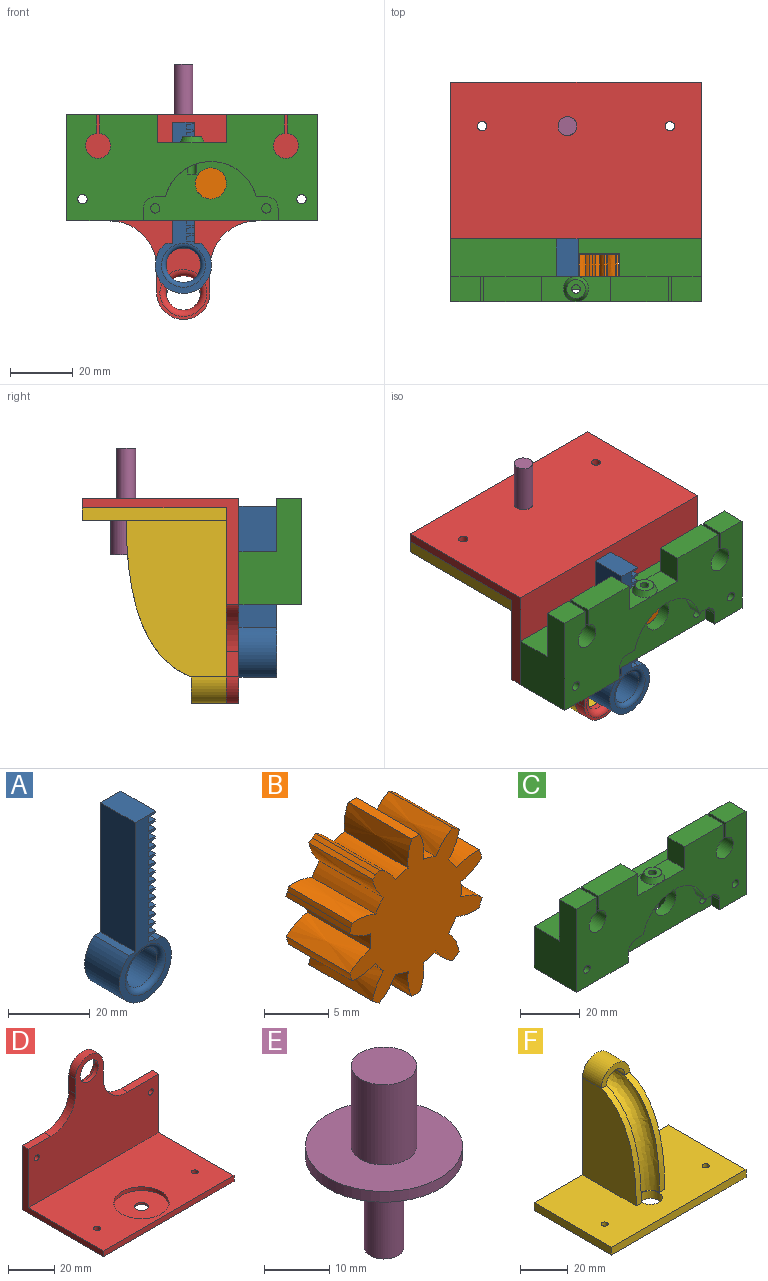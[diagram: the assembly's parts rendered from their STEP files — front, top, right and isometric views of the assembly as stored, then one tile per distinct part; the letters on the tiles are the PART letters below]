
ASSEMBLY  parts=6 mates=12
PART A: 71 faces, bbox 18x12x54.7 mm
  f0: plane 38.7x12mm, normal (1,0,0), area 228.2mm2, adj f1,f2,f4,f5,f6,f8,f9,f10
  f1: plane 54.7x18mm, normal (0,-1,0), area 288.5mm2, adj f0,f3,f4,f5,f6,f7,f9,f10
  f2: plane 54.7x18mm, normal (0,1,0), area 356mm2, adj f0,f3,f4,f65,f66,f68,f70
  f3: plane 38.7x12mm, normal (-1,0,0), area 464.4mm2, adj f1,f2,f4,f65
  f4: plane 12x7mm, normal (0,0,1), area 84mm2, adj f0,f1,f2,f3
  f5: plane 7.5x2.5mm, normal (0.12,0,0.99), area 18.9mm2, adj f0,f1,f7,f8
  f6: plane 7.5x2.5mm, normal (0.12,0,-0.99), area 18.9mm2, adj f0,f1,f7,f8
  f7: plane 7.5x1.5mm, normal (1,0,0), area 11.2mm2, adj f1,f5,f6,f8
  f8: plane 2.5x2.1mm, normal (0,-1,0), area 4.5mm2, adj f0,f5,f6,f7
  f9: plane 7.5x2.5mm, normal (0.12,0,0.99), area 18.9mm2, adj f0,f1,f11,f12
  f10: plane 7.5x2.5mm, normal (0.12,0,-0.99), area 18.9mm2, adj f0,f1,f11,f12
  f11: plane 7.5x1.5mm, normal (1,0,0), area 11.2mm2, adj f1,f9,f10,f12
  f12: plane 2.5x2.1mm, normal (0,-1,0), area 4.5mm2, adj f0,f9,f10,f11
  f13: plane 7.5x2.5mm, normal (0.12,0,0.99), area 18.9mm2, adj f0,f1,f15,f16
  f14: plane 7.5x2.5mm, normal (0.12,0,-0.99), area 18.9mm2, adj f0,f1,f15,f16
  f15: plane 7.5x1.5mm, normal (1,0,0), area 11.2mm2, adj f1,f13,f14,f16
  f16: plane 2.5x2.1mm, normal (0,-1,0), area 4.5mm2, adj f0,f13,f14,f15
  f17: plane 7.5x2.5mm, normal (0.12,0,0.99), area 18.9mm2, adj f0,f1,f19,f20
  f18: plane 7.5x2.5mm, normal (0.12,0,-0.99), area 18.9mm2, adj f0,f1,f19,f20
  f19: plane 7.5x1.5mm, normal (1,0,0), area 11.3mm2, adj f1,f17,f18,f20
  f20: plane 2.5x2.1mm, normal (0,-1,0), area 4.5mm2, adj f0,f17,f18,f19
  f21: plane 7.5x2.5mm, normal (0.12,0,0.99), area 18.9mm2, adj f0,f1,f23,f24
  f22: plane 7.5x2.5mm, normal (0.12,0,-0.99), area 18.9mm2, adj f0,f1,f23,f24
  f23: plane 7.5x1.5mm, normal (1,0,0), area 11.2mm2, adj f1,f21,f22,f24
  f24: plane 2.5x2.1mm, normal (0,-1,0), area 4.5mm2, adj f0,f21,f22,f23
  f25: plane 7.5x2.5mm, normal (0.12,0,0.99), area 18.9mm2, adj f0,f1,f27,f28
  f26: plane 7.5x2.5mm, normal (0.12,0,-0.99), area 18.9mm2, adj f0,f1,f27,f28
  f27: plane 7.5x1.5mm, normal (1,0,0), area 11.2mm2, adj f1,f25,f26,f28
  f28: plane 2.5x2.1mm, normal (0,-1,0), area 4.5mm2, adj f0,f25,f26,f27
  f29: plane 7.5x2.5mm, normal (0.12,0,0.99), area 18.9mm2, adj f0,f1,f31,f32
  f30: plane 7.5x2.5mm, normal (0.12,0,-0.99), area 18.9mm2, adj f0,f1,f31,f32
  f31: plane 7.5x1.5mm, normal (1,0,0), area 11.3mm2, adj f1,f29,f30,f32
  f32: plane 2.5x2.1mm, normal (0,-1,0), area 4.5mm2, adj f0,f29,f30,f31
  f33: plane 7.5x2.5mm, normal (0.12,0,0.99), area 18.9mm2, adj f0,f1,f35,f36
  f34: plane 7.5x2.5mm, normal (0.12,0,-0.99), area 18.9mm2, adj f0,f1,f35,f36
  f35: plane 7.5x1.5mm, normal (1,0,0), area 11.3mm2, adj f1,f33,f34,f36
  f36: plane 2.5x2.1mm, normal (0,-1,0), area 4.5mm2, adj f0,f33,f34,f35
  f37: plane 7.5x2.5mm, normal (0.12,0,0.99), area 18.9mm2, adj f0,f1,f39,f40
  f38: plane 7.5x2.5mm, normal (0.12,0,-0.99), area 18.9mm2, adj f0,f1,f39,f40
  f39: plane 7.5x1.5mm, normal (1,0,0), area 11.3mm2, adj f1,f37,f38,f40
  f40: plane 2.5x2.1mm, normal (0,-1,0), area 4.5mm2, adj f0,f37,f38,f39
  f41: plane 7.5x2.5mm, normal (0.12,0,0.99), area 18.9mm2, adj f0,f1,f43,f44
  f42: plane 7.5x2.5mm, normal (0.12,0,-0.99), area 18.9mm2, adj f0,f1,f43,f44
  f43: plane 7.5x1.5mm, normal (1,0,0), area 11.3mm2, adj f1,f41,f42,f44
  f44: plane 2.5x2.1mm, normal (0,-1,0), area 4.5mm2, adj f0,f41,f42,f43
  f45: plane 7.5x2.5mm, normal (0.12,0,0.99), area 18.9mm2, adj f0,f1,f47,f48
  f46: plane 7.5x2.5mm, normal (0.12,0,-0.99), area 18.9mm2, adj f0,f1,f47,f48
  f47: plane 7.5x1.5mm, normal (1,0,0), area 11.3mm2, adj f1,f45,f46,f48
  f48: plane 2.5x2.1mm, normal (0,-1,0), area 4.5mm2, adj f0,f45,f46,f47
  f49: plane 7.5x2.5mm, normal (0.12,0,0.99), area 18.9mm2, adj f0,f1,f51,f52
  f50: plane 7.5x2.5mm, normal (0.12,0,-0.99), area 18.9mm2, adj f0,f1,f51,f52
  f51: plane 7.5x1.5mm, normal (1,0,0), area 11.3mm2, adj f1,f49,f50,f52
  f52: plane 2.5x2.1mm, normal (0,-1,0), area 4.5mm2, adj f0,f49,f50,f51
  f53: plane 7.5x2.5mm, normal (0.12,0,0.99), area 18.9mm2, adj f0,f1,f55,f56
  f54: plane 7.5x2.5mm, normal (0.12,0,-0.99), area 18.9mm2, adj f0,f1,f55,f56
  f55: plane 7.5x1.5mm, normal (1,0,0), area 11.2mm2, adj f1,f53,f54,f56
  f56: plane 2.5x2.1mm, normal (0,-1,0), area 4.5mm2, adj f0,f53,f54,f55
  f57: plane 7.5x2.5mm, normal (0.12,0,0.99), area 18.9mm2, adj f0,f1,f59,f60
  f58: plane 7.5x2.5mm, normal (0.12,0,-0.99), area 18.9mm2, adj f0,f1,f59,f60
  f59: plane 7.5x1.5mm, normal (1,0,0), area 11.3mm2, adj f1,f57,f58,f60
  f60: plane 2.5x2.1mm, normal (0,-1,0), area 4.5mm2, adj f0,f57,f58,f59
  f61: plane 7.5x2.5mm, normal (0.12,0,0.99), area 18.9mm2, adj f0,f1,f63,f64
  f62: plane 7.5x2.5mm, normal (0.12,0,-0.99), area 18.9mm2, adj f0,f1,f63,f64
  f63: plane 7.5x1.5mm, normal (1,0,0), area 11.2mm2, adj f1,f61,f62,f64
  f64: plane 2.5x2.1mm, normal (0,-1,0), area 4.5mm2, adj f0,f61,f62,f63
  f65: plane 12x2.16mm, normal (0,0,1), area 25.9mm2, adj f1,f2,f3,f68
  f66: plane 12x2.16mm, normal (0,0,1), area 25.9mm2, adj f0,f1,f2,f68
  f67: cylinder r=5.5mm len=11mm, axis (0,-1,0), area 311mm2, adj f69,f70
  f68: cylinder r=9mm len=18mm, axis (0,-1,0), area 531.8mm2, adj f1,f2,f65,f66
  f69: torus R=7mm, axis (0,-1,0), area 89.5mm2, adj f1,f67
  f70: torus R=7mm, axis (0,-1,0), area 89.5mm2, adj f2,f67
PART B: 45 faces, bbox 14.5x7x15 mm
  f0: extruded ~7x2.3mm, area 18.3mm2, adj f1,f42,f43,f44
  f1: cylinder r=7.5mm len=7mm, axis (0,1,0), area 6.4mm2, adj f0,f2,f43,f44
  f2: extruded ~7x1.84mm, area 18.3mm2, adj f1,f3,f43,f44
  f3: cylinder r=5mm len=7mm, axis (0,1,0), area 10mm2, adj f2,f4,f43,f44
  f4: extruded ~7x2.56mm, area 18.3mm2, adj f3,f5,f43,f44
  f5: cylinder r=7.5mm len=7mm, axis (0,1,0), area 6.4mm2, adj f4,f6,f43,f44
  f6: extruded ~7x2.56mm, area 18.3mm2, adj f5,f7,f43,f44
  f7: cylinder r=5mm len=7mm, axis (0,1,0), area 10mm2, adj f6,f8,f43,f44
  f8: extruded ~7x1.84mm, area 18.3mm2, adj f7,f9,f43,f44
  f9: cylinder r=7.5mm len=7mm, axis (0,1,0), area 6.4mm2, adj f8,f10,f43,f44
  f10: extruded ~7x2.3mm, area 18.3mm2, adj f9,f11,f43,f44
  f11: cylinder r=5mm len=7mm, axis (0,1,0), area 10mm2, adj f10,f12,f43,f44
  f12: extruded ~7x2.56mm, area 18.3mm2, adj f11,f13,f43,f44
  f13: cylinder r=7.5mm len=7mm, axis (0,1,0), area 3.2mm2, adj f12,f14,f43,f44
  f14: plane 7x0.43mm, normal (0.95,0,-0.31), area 3.1mm2, adj f13,f15,f43,f44
  f15: extruded ~7x2.32mm, area 18.4mm2, adj f14,f16,f43,f44
  f16: cylinder r=5mm len=7mm, axis (0,1,0), area 10mm2, adj f15,f17,f43,f44
  f17: extruded ~7x2.31mm, area 18.3mm2, adj f16,f18,f43,f44
  f18: cylinder r=7.5mm len=7mm, axis (0,1,0), area 6.4mm2, adj f17,f19,f43,f44
  f19: extruded ~7x2.56mm, area 18.3mm2, adj f18,f20,f43,f44
  f20: cylinder r=5mm len=7mm, axis (0,1,0), area 10mm2, adj f19,f21,f43,f44
  f21: extruded ~7x2.3mm, area 18.3mm2, adj f20,f22,f43,f44
  f22: cylinder r=7.5mm len=7mm, axis (0,1,0), area 6.4mm2, adj f21,f23,f43,f44
  f23: extruded ~7x1.84mm, area 18.3mm2, adj f22,f24,f43,f44
  f24: cylinder r=5mm len=7mm, axis (0,1,0), area 10mm2, adj f23,f25,f43,f44
  f25: extruded ~7x2.57mm, area 18.4mm2, adj f24,f26,f43,f44
  f26: plane 7x0.9mm, normal (0,0,1), area 6.3mm2, adj f25,f27,f43,f44
  f27: extruded ~7x2.57mm, area 18.4mm2, adj f26,f28,f43,f44
  f28: cylinder r=5mm len=7mm, axis (0,1,0), area 10mm2, adj f27,f29,f43,f44
  f29: extruded ~7x1.84mm, area 18.3mm2, adj f28,f30,f43,f44
  f30: cylinder r=7.5mm len=7mm, axis (0,1,0), area 3.2mm2, adj f29,f31,f43,f44
  f31: plane 7x0.36mm, normal (-0.59,0,0.81), area 3.2mm2, adj f30,f32,f43,f44
  f32: extruded ~7x2.32mm, area 18.4mm2, adj f31,f33,f43,f44
  f33: cylinder r=5mm len=7mm, axis (0,1,0), area 10mm2, adj f32,f34,f43,f44
  f34: extruded ~7x2.56mm, area 18.3mm2, adj f33,f35,f43,f44
  f35: cylinder r=7.5mm len=7mm, axis (0,1,0), area 3.2mm2, adj f34,f36,f43,f44
  f36: plane 7x0.43mm, normal (-0.95,0,0.31), area 3.1mm2, adj f35,f37,f43,f44
  f37: extruded ~7x2.32mm, area 18.4mm2, adj f36,f38,f43,f44
  f38: cylinder r=5mm len=7mm, axis (0,1,0), area 10mm2, adj f37,f39,f43,f44
  f39: extruded ~7x2.31mm, area 18.3mm2, adj f38,f40,f43,f44
  f40: cylinder r=7.5mm len=7mm, axis (0,1,0), area 6.4mm2, adj f39,f41,f43,f44
  f41: extruded ~7x2.56mm, area 18.3mm2, adj f40,f42,f43,f44
  f42: cylinder r=5mm len=7mm, axis (0,1,0), area 10mm2, adj f0,f41,f43,f44
  f43: plane 15x14.54mm, normal (0,-1,0), area 117.2mm2, adj f0,f1,f2,f3,f4,f5,f6,f7
  f44: plane 15x14.54mm, normal (0,1,0), area 117.2mm2, adj f0,f1,f2,f3,f4,f5,f6,f7
PART C: 47 faces, bbox 80x20x34 mm
  f0: plane 80x34mm, normal (0,-1,0), area 1826mm2, adj f1,f4,f5,f6,f7,f8,f9,f10
  f1: plane 11x8mm, normal (0,0,1), area 62.9mm2, adj f0,f2,f13,f42
  f2: plane 80x34mm, normal (0,1,0), area 1315.2mm2, adj f1,f4,f5,f6,f7,f8,f9,f10
  f3: plane 43x19mm, normal (0,-1,0), area 469.2mm2, adj f4,f20,f21,f22,f23,f24,f25,f26
  f4: plane 80x20mm, normal (0,0,-1), area 1244.6mm2, adj f0,f2,f3,f5,f19,f20,f26,f31
  f5: plane 34x20mm, normal (1,0,0), area 476mm2, adj f0,f2,f4,f6,f35,f39
  f6: plane 9.5x8mm, normal (0,0,1), area 76mm2, adj f0,f2,f5,f7
  f7: plane 8x6.03mm, normal (-1,0,0), area 48.3mm2, adj f0,f2,f6,f8
  f8: cylinder r=4mm len=8mm, axis (0,1,0), area 193mm2, adj f0,f2,f7,f9
  f9: plane 8x6.03mm, normal (1,0,0), area 48.3mm2, adj f0,f2,f8,f10
  f10: plane 18.5x8mm, normal (0,0,1), area 148mm2, adj f0,f2,f9,f11
  f11: plane 9x8mm, normal (-1,0,0), area 72mm2, adj f0,f2,f10,f12
  f12: plane 11x8mm, normal (0,0,1), area 62.9mm2, adj f0,f2,f11,f42
  f13: plane 9x8mm, normal (1,0,0), area 72mm2, adj f0,f1,f2,f14
  f14: plane 18.5x8mm, normal (0,0,1), area 148mm2, adj f0,f2,f13,f15
  f15: plane 8x6.03mm, normal (-1,0,0), area 48.3mm2, adj f0,f2,f14,f16
  f16: cylinder r=4mm len=8mm, axis (0,1,0), area 193mm2, adj f0,f2,f15,f17
  f17: plane 8x6.03mm, normal (1,0,0), area 48.3mm2, adj f0,f2,f16,f18
  f18: plane 9.5x8mm, normal (0,0,1), area 76mm2, adj f0,f2,f17,f19
  f19: plane 34x20mm, normal (-1,0,0), area 476mm2, adj f0,f2,f4,f18,f30,f31
  f20: plane 4x4mm, normal (-1,0,0), area 16mm2, adj f0,f3,f4,f21
  f21: cylinder r=3.75mm len=4mm, axis (0,-1,0), area 23.6mm2, adj f0,f3,f20,f22
  f22: plane 4x3.23mm, normal (0,0,-1), area 12.9mm2, adj f0,f3,f21,f23
  f23: cylinder r=15mm len=29.05mm, axis (0,-1,0), area 154.9mm2, adj f0,f3,f22,f24,f43
  f24: plane 4x3.23mm, normal (0,0,-1), area 12.9mm2, adj f0,f3,f23,f25
  f25: cylinder r=3.75mm len=4mm, axis (0,-1,0), area 23.6mm2, adj f0,f3,f24,f26
  f26: plane 4x4mm, normal (1,0,0), area 16mm2, adj f0,f3,f4,f25
  f27: cylinder r=5mm len=10mm, axis (0,-1,0), area 125.7mm2, adj f2,f3
  f28: cylinder r=1.5mm len=4mm, axis (0,-1,0), area 37.7mm2, adj f3,f34
  f29: cylinder r=1.5mm len=4mm, axis (0,-1,0), area 37.7mm2, adj f3,f33
  f30: plane 33.75x12mm, normal (0,0,1), area 405mm2, adj f2,f19,f31,f32
  f31: plane 33.75x17mm, normal (0,1,0), area 566.7mm2, adj f4,f19,f30,f32,f46
  f32: plane 17x12mm, normal (1,0,0), area 204mm2, adj f2,f4,f30,f31
  f33: plane 3x3mm, normal (0,-1,0), area 7.1mm2, adj f29
  f34: plane 3x3mm, normal (0,-1,0), area 7.1mm2, adj f28
  f35: plane 39.25x17mm, normal (0,1,0), area 631.9mm2, adj f4,f5,f36,f39,f40,f45
  f36: plane 17x4.5mm, normal (-1,0,0), area 76.5mm2, adj f4,f35,f37,f39
  f37: plane 17x13.25mm, normal (0,-1,0), area 197mm2, adj f4,f36,f38,f39,f40
  f38: plane 17x7.5mm, normal (-1,0,0), area 127.5mm2, adj f2,f4,f37,f39
  f39: plane 39.25x12mm, normal (0,0,1), area 371.6mm2, adj f2,f5,f35,f36,f37,f38
  f40: cylinder r=3mm len=6mm, axis (0,-1,0), area 84.8mm2, adj f35,f37
  f41: plane 6x6mm, normal (0,0,1), area 22.3mm2, adj f42,f43
  f42: cone r=3mm half-angle=26.6deg, axis (0,0,-1), area 49.2mm2, adj f1,f12,f41
  f43: cylinder r=1.38mm len=12mm, axis (0,0,1), area 92mm2, adj f3,f23,f41,f44
  f44: plane 2.75x1.38mm, normal (0,0,1), area 3mm2, adj f3,f43
  f45: cylinder r=1.5mm len=20mm, axis (0,-1,0), area 188.5mm2, adj f0,f35
  f46: cylinder r=1.5mm len=20mm, axis (0,-1,0), area 188.5mm2, adj f0,f31
PART D: 23 faces, bbox 80x50x66.7 mm
  f0: plane 19.25x4mm, normal (0,0,1), area 77mm2, adj f1,f2,f5,f21
  f1: plane 80x65.5mm, normal (0,1,0), area 3130.2mm2, adj f0,f5,f8,f10,f11,f14,f15,f16
  f2: plane 80x62.5mm, normal (0,-1,0), area 2971.9mm2, adj f0,f5,f8,f9,f11,f14,f15,f16
  f3: cylinder r=3mm len=6mm, axis (0,0,-1), area 18.8mm2, adj f10,f13
  f4: plane 80x3mm, normal (0,-1,0), area 240mm2, adj f5,f8,f9,f10
  f5: plane 50x34mm, normal (1,0,0), area 274mm2, adj f0,f1,f2,f4,f9,f10
  f6: cylinder r=1.5mm len=3mm, axis (0,0,-1), area 28.3mm2, adj f9,f10
  f7: cylinder r=1.5mm len=3mm, axis (0,0,-1), area 28.3mm2, adj f9,f10
  f8: plane 50x34mm, normal (-1,0,0), area 274mm2, adj f1,f2,f4,f9,f10,f11
  f9: plane 80x46mm, normal (0,0,1), area 3213.5mm2, adj f2,f4,f5,f6,f7,f8,f12
  f10: plane 80x50mm, normal (0,0,-1), area 3957.6mm2, adj f1,f3,f4,f5,f6,f7,f8
  f11: plane 13.75x4mm, normal (0,0,1), area 55mm2, adj f1,f2,f8,f20
  f12: cylinder r=12mm len=24mm, axis (0,0,1), area 150.8mm2, adj f9,f13
  f13: plane 24x24mm, normal (0,0,1), area 424.1mm2, adj f3,f12
  f14: cylinder r=1.5mm len=4mm, axis (0,1,0), area 37.7mm2, adj f1,f2
  f15: cylinder r=1.5mm len=4mm, axis (0,1,0), area 37.7mm2, adj f1,f2
  f16: plane 8x4mm, normal (1,0,0), area 32mm2, adj f1,f2,f17,f21
  f17: cylinder r=8.5mm len=17mm, axis (0,-1,0), area 106.8mm2, adj f1,f2,f16,f18
  f18: plane 8x4mm, normal (-1,0,0), area 32mm2, adj f1,f2,f17,f20
  f19: cylinder r=5.5mm len=11mm, axis (0,-1,0), area 69.1mm2, adj f2,f22
  f20: cylinder r=15mm len=15mm, axis (0,1,0), area 94.2mm2, adj f1,f2,f11,f18
  f21: cylinder r=15mm len=15mm, axis (0,-1,0), area 94.2mm2, adj f0,f1,f2,f16
  f22: torus R=7.5mm, axis (0,-1,0), area 122.9mm2, adj f1,f19
PART E: 7 faces, bbox 24x24x34 mm
  f0: plane 10x10mm, normal (0,0,1), area 78.5mm2, adj f6
  f1: plane 6x6mm, normal (0,0,-1), area 28.3mm2, adj f2
  f2: cylinder r=3mm len=17mm, axis (0,0,-1), area 320.4mm2, adj f1,f3
  f3: plane 24x24mm, normal (0,0,-1), area 424.1mm2, adj f2,f4
  f4: cylinder r=12mm len=24mm, axis (0,0,-1), area 150.8mm2, adj f3,f5
  f5: plane 24x24mm, normal (0,0,1), area 373.8mm2, adj f4,f6
  f6: cylinder r=5mm len=15mm, axis (0,0,-1), area 471.2mm2, adj f0,f5
PART F: 19 faces, bbox 80x46x62.5 mm
  f0: plane 11.32x3.31mm, normal (0,0,1), area 0.9mm2, adj f1,f2,f15,f17,f18
  f1: extruded ~50x20.68mm, area 175.5mm2, adj f0,f2,f5,f15
  f2: plane 52x32mm, normal (1,0,0), area 1371.2mm2, adj f0,f1,f5,f7,f16
  f3: plane 52x32mm, normal (-1,0,0), area 1371.2mm2, adj f4,f5,f7,f14,f16
  f4: plane 11.32x3.31mm, normal (0,0,1), area 0.9mm2, adj f3,f14,f15,f17,f18
  f5: plane 80x46mm, normal (0,0,1), area 3090.8mm2, adj f1,f2,f3,f6,f7,f8,f9,f10
  f6: plane 46x4mm, normal (1,0,0), area 184mm2, adj f5,f7,f11,f13
  f7: plane 80x62.5mm, normal (0,1,0), area 1188.5mm2, adj f2,f3,f5,f6,f8,f13,f15,f16
  f8: plane 46x4mm, normal (-1,0,0), area 184mm2, adj f5,f7,f11,f13
  f9: cylinder r=1.5mm len=4mm, axis (0,0,-1), area 37.7mm2, adj f5,f13
  f10: cylinder r=1.5mm len=4mm, axis (0,0,-1), area 37.7mm2, adj f5,f13
  f11: plane 80x4mm, normal (0,-1,0), area 320mm2, adj f5,f6,f8,f13
  f12: cylinder r=5mm len=10mm, axis (0,0,-1), area 125.7mm2, adj f5,f13
  f13: plane 80x46mm, normal (0,0,-1), area 3587.3mm2, adj f6,f7,f8,f9,f10,f11,f12
  f14: extruded ~50x20.68mm, area 175.5mm2, adj f3,f4,f5,f15
  f15: bspline ~55.5x37.5mm, area 1142.3mm2, adj f0,f1,f4,f5,f7,f14
  f16: cylinder r=8.5mm len=17mm, axis (0,1,0), area 300.4mm2, adj f2,f3,f7,f18
  f17: cylinder r=5.5mm len=11.25mm, axis (0,1,0), area 194.4mm2, adj f0,f4,f7,f18
  f18: plane 17x8.5mm, normal (0,-1,0), area 66mm2, adj f0,f4,f16,f17
PLACE A t=(-3.95,7.91,-17.26)mm
PLACE B rot(axis=(0,-1,0),152.5deg) t=(4.8,8.91,1.9)mm
PLACE C t=(-1.2,1.91,6.9)mm fixed
PLACE D rot(axis=(-1,0,0),180deg) t=(-1.2,49.91,23.9)mm
PLACE E rot(axis=(-0.58,0.81,0),180deg) t=(-3.95,49.91,5.9)mm
PLACE F rot(axis=(1,0,0),180deg) t=(-1.2,40.91,20.9)mm
MATE planar A.f1 <-> C.f2  axis (0,-1,0) through (-4.49,1.91,-6.1)mm
MATE planar D.f1 <-> C.f31  axis (0,-1,0) through (-1.57,13.91,3.43)mm
MATE planar D.f8 <-> C.f19  axis (-1,0,0) through (-41.2,17.91,5.4)mm
MATE planar B.f42 <-> C.f2  axis (0,-1,0) through (4.8,1.91,1.9)mm
MATE planar F.f8 <-> D.f8  axis (-1,0,0) through (-41.2,40.91,18.9)mm
MATE cylindrical B.f1 <-> C.f27  axis (0,1,0) through (4.8,8.91,1.9)mm
MATE cylindrical E.f2 <-> F.f12  axis (0,0,1) through (-3.95,49.91,13.4)mm
MATE planar D.f10 <-> C.f18  axis (0,0,1) through (-1.18,38.79,23.9)mm
MATE planar E.f2 <-> D.f3  axis (0,0,1) through (-3.95,49.91,22.9)mm
MATE planar A.f0 <-> C.f36  axis (1,0,0) through (-0.45,10.24,2.09)mm
MATE cylindrical F.f10 <-> D.f6  axis (0,0,1) through (-31.2,49.91,18.9)mm
MATE planar F.f13 <-> D.f9  axis (0,0,1) through (-1.14,40.67,20.9)mm
